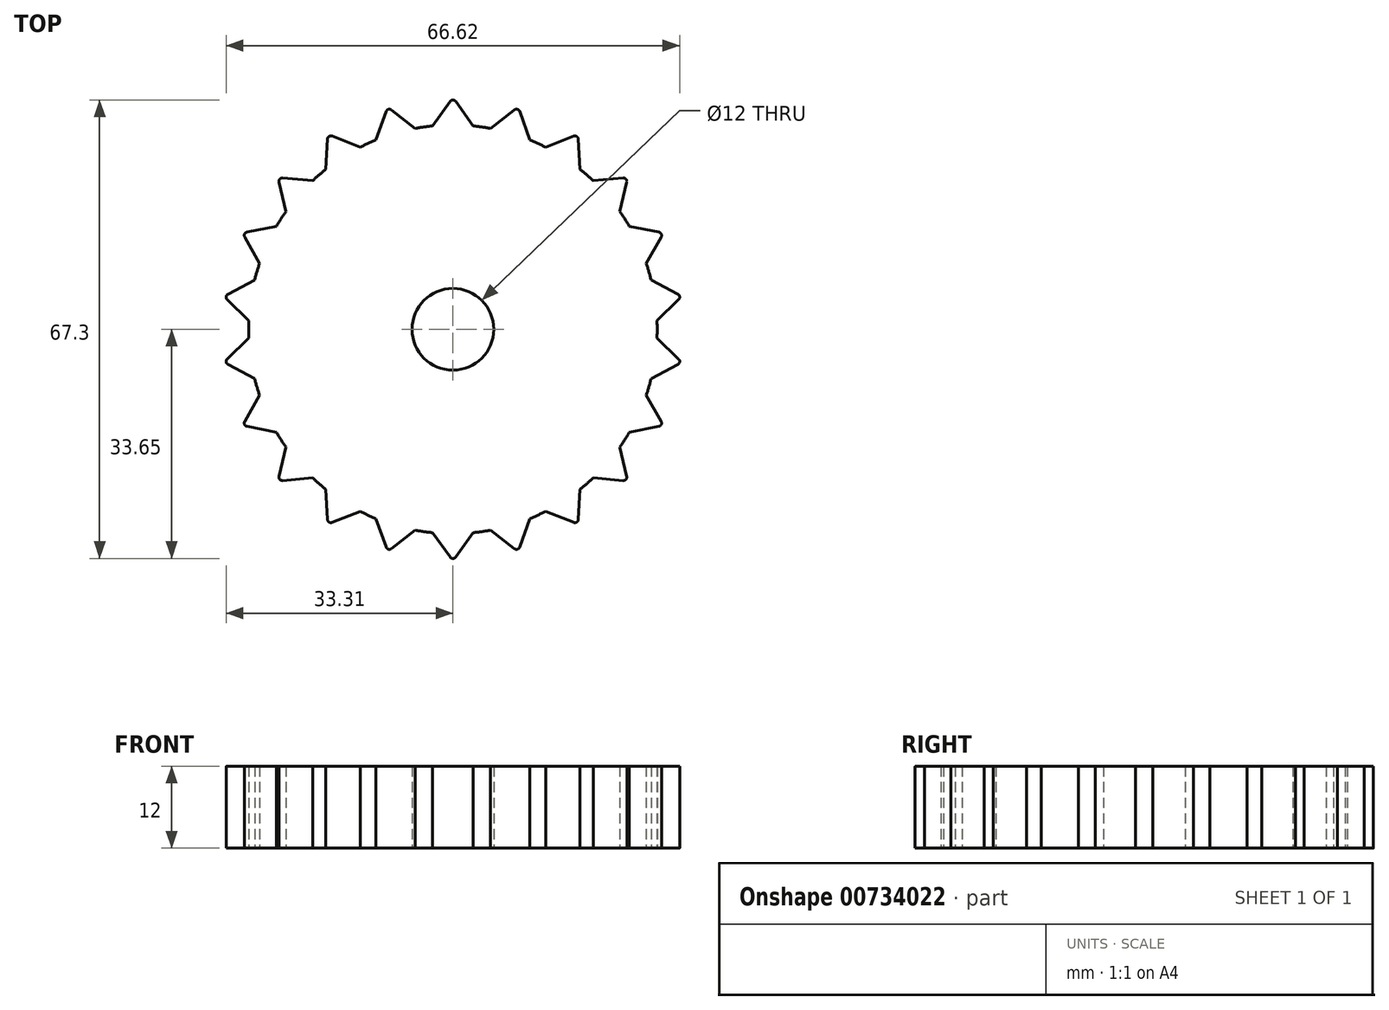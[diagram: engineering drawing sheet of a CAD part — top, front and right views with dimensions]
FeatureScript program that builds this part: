
annotation { "Feature Type Name" : "Feature", "Feature Type Description" : "" }
export const myFeature = defineFeature(function(context is Context, id is Id, definition is map)
    precondition{}
    {
        {
            var Q0;
            Q0=qCreatedBy(makeId("Top.planeOp"),FACE);
            var sketch = newSketch(context, id + "F0", { "sketchPlane" : qUnion([Q0])});
            skArc(sketch, "E0", {"start": v(-24.52, 17.28) * mm, "mid": v(-25.24, 16.22) * mm, "end": v(-25.9, 15.13) * mm});
            skLineSegment(sketch, "E1", {"start": v(-3, 29.85) * mm, "end": v(-0.4, 33.44) * mm});
            skLineSegment(sketch, "E2", {"start": v(0.4, 33.44) * mm, "end": v(3, 29.85) * mm});
            skPoint(sketch, "E3.visualSharp", {"position": v(0, 34) * mm});
            skArc(sketch, "E3.filletArc", {"start": v(0.4, 33.44) * mm, "mid": v(0, 33.65) * mm, "end": v(-0.4, 33.44) * mm});
            skLineSegment(sketch, "E4.1.0", {"start": v(-11.29, 27.8) * mm, "end": v(-9.8, 31.97) * mm});
            skLineSegment(sketch, "E4.1.1", {"start": v(-9.03, 32.2) * mm, "end": v(-5.53, 29.49) * mm});
            skPoint(sketch, "E4.1.2", {"position": v(-9.58, 32.62) * mm});
            skArc(sketch, "E4.1.3", {"start": v(-9.03, 32.2) * mm, "mid": v(-9.48, 32.28) * mm, "end": v(-9.8, 31.97) * mm});
            skLineSegment(sketch, "E4.2.0", {"start": v(-18.66, 23.49) * mm, "end": v(-18.42, 27.91) * mm});
            skLineSegment(sketch, "E4.2.1", {"start": v(-17.74, 28.35) * mm, "end": v(-13.61, 26.73) * mm});
            skPoint(sketch, "E4.2.2", {"position": v(-18.38, 28.6) * mm});
            skArc(sketch, "E4.2.3", {"start": v(-17.74, 28.35) * mm, "mid": v(-18.2, 28.3) * mm, "end": v(-18.42, 27.91) * mm});
            skLineSegment(sketch, "E4.3.0", {"start": v(-24.52, 17.28) * mm, "end": v(-25.54, 21.6) * mm});
            skLineSegment(sketch, "E4.3.1", {"start": v(-25, 22.2) * mm, "end": v(-20.6, 21.81) * mm});
            skPoint(sketch, "E4.3.2", {"position": v(-25.7, 22.27) * mm});
            skArc(sketch, "E4.3.3", {"start": v(-25, 22.2) * mm, "mid": v(-25.43, 22.03) * mm, "end": v(-25.54, 21.6) * mm});
            skLineSegment(sketch, "E4.4.0", {"start": v(-28.4, 9.67) * mm, "end": v(-30.59, 13.52) * mm});
            skLineSegment(sketch, "E4.4.1", {"start": v(-30.25, 14.26) * mm, "end": v(-25.9, 15.13) * mm});
            skPoint(sketch, "E4.4.2", {"position": v(-30.93, 14.12) * mm});
            skArc(sketch, "E4.4.3", {"start": v(-30.25, 14.26) * mm, "mid": v(-30.6, 13.98) * mm, "end": v(-30.59, 13.52) * mm});
            skLineSegment(sketch, "E4.5.0", {"start": v(-29.97, 1.28) * mm, "end": v(-33.16, 4.36) * mm});
            skLineSegment(sketch, "E4.5.1", {"start": v(-33.04, 5.16) * mm, "end": v(-29.12, 7.22) * mm});
            skPoint(sketch, "E4.5.2", {"position": v(-33.65, 4.84) * mm});
            skArc(sketch, "E4.5.3", {"start": v(-33.04, 5.16) * mm, "mid": v(-33.3, 4.79) * mm, "end": v(-33.16, 4.36) * mm});
            skLineSegment(sketch, "E4.6.0", {"start": v(-29.12, -7.22) * mm, "end": v(-33.04, -5.16) * mm});
            skLineSegment(sketch, "E4.6.1", {"start": v(-33.16, -4.36) * mm, "end": v(-29.97, -1.28) * mm});
            skPoint(sketch, "E4.6.2", {"position": v(-33.65, -4.84) * mm});
            skArc(sketch, "E4.6.3", {"start": v(-33.16, -4.36) * mm, "mid": v(-33.3, -4.79) * mm, "end": v(-33.04, -5.16) * mm});
            skLineSegment(sketch, "E4.7.0", {"start": v(-25.9, -15.13) * mm, "end": v(-30.25, -14.26) * mm});
            skLineSegment(sketch, "E4.7.1", {"start": v(-30.59, -13.52) * mm, "end": v(-28.4, -9.67) * mm});
            skPoint(sketch, "E4.7.2", {"position": v(-30.93, -14.12) * mm});
            skArc(sketch, "E4.7.3", {"start": v(-30.59, -13.52) * mm, "mid": v(-30.6, -13.98) * mm, "end": v(-30.25, -14.26) * mm});
            skLineSegment(sketch, "E4.8.0", {"start": v(-20.6, -21.81) * mm, "end": v(-25, -22.2) * mm});
            skLineSegment(sketch, "E4.8.1", {"start": v(-25.54, -21.6) * mm, "end": v(-24.52, -17.28) * mm});
            skPoint(sketch, "E4.8.2", {"position": v(-25.7, -22.27) * mm});
            skArc(sketch, "E4.8.3", {"start": v(-25.54, -21.6) * mm, "mid": v(-25.43, -22.03) * mm, "end": v(-25, -22.2) * mm});
            skLineSegment(sketch, "E4.9.0", {"start": v(-13.61, -26.73) * mm, "end": v(-17.74, -28.35) * mm});
            skLineSegment(sketch, "E4.9.1", {"start": v(-18.42, -27.91) * mm, "end": v(-18.66, -23.49) * mm});
            skPoint(sketch, "E4.9.2", {"position": v(-18.38, -28.6) * mm});
            skArc(sketch, "E4.9.3", {"start": v(-18.42, -27.91) * mm, "mid": v(-18.2, -28.3) * mm, "end": v(-17.74, -28.35) * mm});
            skLineSegment(sketch, "E4.10.0", {"start": v(-5.53, -29.49) * mm, "end": v(-9.03, -32.2) * mm});
            skLineSegment(sketch, "E4.10.1", {"start": v(-9.8, -31.97) * mm, "end": v(-11.29, -27.8) * mm});
            skPoint(sketch, "E4.10.2", {"position": v(-9.58, -32.62) * mm});
            skArc(sketch, "E4.10.3", {"start": v(-9.8, -31.97) * mm, "mid": v(-9.48, -32.28) * mm, "end": v(-9.03, -32.2) * mm});
            skLineSegment(sketch, "E4.11.0", {"start": v(3, -29.85) * mm, "end": v(0.4, -33.44) * mm});
            skLineSegment(sketch, "E4.11.1", {"start": v(-0.4, -33.44) * mm, "end": v(-3, -29.85) * mm});
            skPoint(sketch, "E4.11.2", {"position": v(0, -34) * mm});
            skArc(sketch, "E4.11.3", {"start": v(-0.4, -33.44) * mm, "mid": v(0, -33.65) * mm, "end": v(0.4, -33.44) * mm});
            skLineSegment(sketch, "E4.12.0", {"start": v(11.29, -27.8) * mm, "end": v(9.8, -31.97) * mm});
            skLineSegment(sketch, "E4.12.1", {"start": v(9.03, -32.2) * mm, "end": v(5.53, -29.49) * mm});
            skPoint(sketch, "E4.12.2", {"position": v(9.58, -32.62) * mm});
            skArc(sketch, "E4.12.3", {"start": v(9.03, -32.2) * mm, "mid": v(9.48, -32.28) * mm, "end": v(9.8, -31.97) * mm});
            skLineSegment(sketch, "E4.13.0", {"start": v(18.66, -23.49) * mm, "end": v(18.42, -27.91) * mm});
            skLineSegment(sketch, "E4.13.1", {"start": v(17.74, -28.35) * mm, "end": v(13.61, -26.73) * mm});
            skPoint(sketch, "E4.13.2", {"position": v(18.38, -28.6) * mm});
            skArc(sketch, "E4.13.3", {"start": v(17.74, -28.35) * mm, "mid": v(18.2, -28.3) * mm, "end": v(18.42, -27.91) * mm});
            skLineSegment(sketch, "E4.14.0", {"start": v(24.52, -17.28) * mm, "end": v(25.54, -21.6) * mm});
            skLineSegment(sketch, "E4.14.1", {"start": v(25, -22.2) * mm, "end": v(20.6, -21.81) * mm});
            skPoint(sketch, "E4.14.2", {"position": v(25.7, -22.27) * mm});
            skArc(sketch, "E4.14.3", {"start": v(25, -22.2) * mm, "mid": v(25.43, -22.03) * mm, "end": v(25.54, -21.6) * mm});
            skLineSegment(sketch, "E4.15.0", {"start": v(28.4, -9.67) * mm, "end": v(30.59, -13.52) * mm});
            skLineSegment(sketch, "E4.15.1", {"start": v(30.25, -14.26) * mm, "end": v(25.9, -15.13) * mm});
            skPoint(sketch, "E4.15.2", {"position": v(30.93, -14.12) * mm});
            skArc(sketch, "E4.15.3", {"start": v(30.25, -14.26) * mm, "mid": v(30.6, -13.98) * mm, "end": v(30.59, -13.52) * mm});
            skLineSegment(sketch, "E4.16.0", {"start": v(29.97, -1.28) * mm, "end": v(33.16, -4.36) * mm});
            skLineSegment(sketch, "E4.16.1", {"start": v(33.04, -5.16) * mm, "end": v(29.12, -7.22) * mm});
            skPoint(sketch, "E4.16.2", {"position": v(33.65, -4.84) * mm});
            skArc(sketch, "E4.16.3", {"start": v(33.04, -5.16) * mm, "mid": v(33.3, -4.79) * mm, "end": v(33.16, -4.36) * mm});
            skLineSegment(sketch, "E4.17.0", {"start": v(29.12, 7.22) * mm, "end": v(33.04, 5.16) * mm});
            skLineSegment(sketch, "E4.17.1", {"start": v(33.16, 4.36) * mm, "end": v(29.97, 1.28) * mm});
            skPoint(sketch, "E4.17.2", {"position": v(33.65, 4.84) * mm});
            skArc(sketch, "E4.17.3", {"start": v(33.16, 4.36) * mm, "mid": v(33.3, 4.79) * mm, "end": v(33.04, 5.16) * mm});
            skLineSegment(sketch, "E4.18.0", {"start": v(25.9, 15.13) * mm, "end": v(30.25, 14.26) * mm});
            skLineSegment(sketch, "E4.18.1", {"start": v(30.59, 13.52) * mm, "end": v(28.4, 9.67) * mm});
            skPoint(sketch, "E4.18.2", {"position": v(30.93, 14.12) * mm});
            skArc(sketch, "E4.18.3", {"start": v(30.59, 13.52) * mm, "mid": v(30.6, 13.98) * mm, "end": v(30.25, 14.26) * mm});
            skLineSegment(sketch, "E4.19.0", {"start": v(20.6, 21.81) * mm, "end": v(25, 22.2) * mm});
            skLineSegment(sketch, "E4.19.1", {"start": v(25.54, 21.6) * mm, "end": v(24.52, 17.28) * mm});
            skPoint(sketch, "E4.19.2", {"position": v(25.7, 22.27) * mm});
            skArc(sketch, "E4.19.3", {"start": v(25.54, 21.6) * mm, "mid": v(25.43, 22.03) * mm, "end": v(25, 22.2) * mm});
            skLineSegment(sketch, "E4.20.0", {"start": v(13.61, 26.73) * mm, "end": v(17.74, 28.35) * mm});
            skLineSegment(sketch, "E4.20.1", {"start": v(18.42, 27.91) * mm, "end": v(18.66, 23.49) * mm});
            skPoint(sketch, "E4.20.2", {"position": v(18.38, 28.6) * mm});
            skArc(sketch, "E4.20.3", {"start": v(18.42, 27.91) * mm, "mid": v(18.2, 28.3) * mm, "end": v(17.74, 28.35) * mm});
            skLineSegment(sketch, "E4.21.0", {"start": v(5.53, 29.49) * mm, "end": v(9.03, 32.2) * mm});
            skLineSegment(sketch, "E4.21.1", {"start": v(9.8, 31.97) * mm, "end": v(11.29, 27.8) * mm});
            skPoint(sketch, "E4.21.2", {"position": v(9.58, 32.62) * mm});
            skArc(sketch, "E4.21.3", {"start": v(9.8, 31.97) * mm, "mid": v(9.48, 32.28) * mm, "end": v(9.03, 32.2) * mm});
            skCircle(sketch, "E5", {"center": v(0, 0) * mm, "radius": 34 * mm, "construction": true});
            skArc(sketch, "E6.trimOffspring", {"start": v(-18.66, 23.49) * mm, "mid": v(-19.65, 22.67) * mm, "end": v(-20.6, 21.81) * mm});
            skArc(sketch, "E7.trimOffspring", {"start": v(-11.29, 27.8) * mm, "mid": v(-12.46, 27.29) * mm, "end": v(-13.61, 26.73) * mm});
            skArc(sketch, "E8.trimOffspring", {"start": v(-3, 29.85) * mm, "mid": v(-4.27, 29.7) * mm, "end": v(-5.53, 29.49) * mm});
            skArc(sketch, "E9.trimOffspring", {"start": v(5.53, 29.49) * mm, "mid": v(4.27, 29.7) * mm, "end": v(3, 29.85) * mm});
            skArc(sketch, "E10.trimOffspring", {"start": v(13.61, 26.73) * mm, "mid": v(12.46, 27.29) * mm, "end": v(11.29, 27.8) * mm});
            skArc(sketch, "E11.trimOffspring", {"start": v(20.6, 21.81) * mm, "mid": v(19.65, 22.67) * mm, "end": v(18.66, 23.49) * mm});
            skArc(sketch, "E12.trimOffspring", {"start": v(25.9, 15.13) * mm, "mid": v(25.24, 16.22) * mm, "end": v(24.52, 17.28) * mm});
            skArc(sketch, "E13.trimOffspring", {"start": v(29.12, 7.22) * mm, "mid": v(28.78, 8.45) * mm, "end": v(28.4, 9.67) * mm});
            skArc(sketch, "E14.trimOffspring", {"start": v(29.97, -1.28) * mm, "mid": v(30, 0) * mm, "end": v(29.97, 1.28) * mm});
            skArc(sketch, "E15.trimOffspring", {"start": v(28.4, -9.67) * mm, "mid": v(28.78, -8.45) * mm, "end": v(29.12, -7.22) * mm});
            skArc(sketch, "E16.trimOffspring", {"start": v(24.52, -17.28) * mm, "mid": v(25.24, -16.22) * mm, "end": v(25.9, -15.13) * mm});
            skArc(sketch, "E17.trimOffspring", {"start": v(18.66, -23.49) * mm, "mid": v(19.65, -22.67) * mm, "end": v(20.6, -21.81) * mm});
            skArc(sketch, "E18.trimOffspring", {"start": v(11.29, -27.8) * mm, "mid": v(12.46, -27.29) * mm, "end": v(13.61, -26.73) * mm});
            skArc(sketch, "E19.trimOffspring", {"start": v(3, -29.85) * mm, "mid": v(4.27, -29.7) * mm, "end": v(5.53, -29.49) * mm});
            skArc(sketch, "E20.trimOffspring", {"start": v(-5.53, -29.49) * mm, "mid": v(-4.27, -29.7) * mm, "end": v(-3, -29.85) * mm});
            skArc(sketch, "E21.trimOffspring", {"start": v(-13.61, -26.73) * mm, "mid": v(-12.46, -27.29) * mm, "end": v(-11.29, -27.8) * mm});
            skArc(sketch, "E22.trimOffspring", {"start": v(-20.6, -21.81) * mm, "mid": v(-19.65, -22.67) * mm, "end": v(-18.66, -23.49) * mm});
            skArc(sketch, "E23.trimOffspring", {"start": v(-25.9, -15.13) * mm, "mid": v(-25.24, -16.22) * mm, "end": v(-24.52, -17.28) * mm});
            skArc(sketch, "E24.trimOffspring", {"start": v(-29.12, -7.22) * mm, "mid": v(-28.78, -8.45) * mm, "end": v(-28.4, -9.67) * mm});
            skArc(sketch, "E25.trimOffspring", {"start": v(-29.97, 1.28) * mm, "mid": v(-30, 0) * mm, "end": v(-29.97, -1.28) * mm});
            skArc(sketch, "E26.trimOffspring", {"start": v(-28.4, 9.67) * mm, "mid": v(-28.78, 8.45) * mm, "end": v(-29.12, 7.22) * mm});
            skSolve(sketch);
        }
        {
            var Q0;
            Q0 = qSketchRegion(id + "F0", true);
            extrude(context, id + "F1", {"entities" : qUnion([Q0]), "endBound" : BoundingType.SYMMETRIC, "depth" : 12 * mm, "offsetDistance" : 25 * mm});
        }
        {
            var Q0;
            Q0=makeQuery(id+"F1.opExtrude","CAP_FACE",FACE,{"disambiguationData":[OSD([sQuery(id+"F0.wireOp",EDGE,"E0"),sQuery(id+"F0.wireOp",EDGE,"E1"),sQuery(id+"F0.wireOp",EDGE,"E2"),sQuery(id+"F0.wireOp",EDGE,"E3.filletArc"),sQuery(id+"F0.wireOp",EDGE,"E4.1.0"),sQuery(id+"F0.wireOp",EDGE,"E4.1.1"),sQuery(id+"F0.wireOp",EDGE,"E4.1.3"),sQuery(id+"F0.wireOp",EDGE,"E4.2.0"),sQuery(id+"F0.wireOp",EDGE,"E4.2.1"),sQuery(id+"F0.wireOp",EDGE,"E4.2.3"),sQuery(id+"F0.wireOp",EDGE,"E4.3.0"),sQuery(id+"F0.wireOp",EDGE,"E4.3.1"),sQuery(id+"F0.wireOp",EDGE,"E4.3.3"),sQuery(id+"F0.wireOp",EDGE,"E4.4.0"),sQuery(id+"F0.wireOp",EDGE,"E4.4.1"),sQuery(id+"F0.wireOp",EDGE,"E4.4.3"),sQuery(id+"F0.wireOp",EDGE,"E4.5.0"),sQuery(id+"F0.wireOp",EDGE,"E4.5.1"),sQuery(id+"F0.wireOp",EDGE,"E4.5.3"),sQuery(id+"F0.wireOp",EDGE,"E4.6.0"),sQuery(id+"F0.wireOp",EDGE,"E4.6.1"),sQuery(id+"F0.wireOp",EDGE,"E4.6.3"),sQuery(id+"F0.wireOp",EDGE,"E4.7.0"),sQuery(id+"F0.wireOp",EDGE,"E4.7.1"),sQuery(id+"F0.wireOp",EDGE,"E4.7.3"),sQuery(id+"F0.wireOp",EDGE,"E4.8.0"),sQuery(id+"F0.wireOp",EDGE,"E4.8.1"),sQuery(id+"F0.wireOp",EDGE,"E4.8.3"),sQuery(id+"F0.wireOp",EDGE,"E4.9.0"),sQuery(id+"F0.wireOp",EDGE,"E4.9.1"),sQuery(id+"F0.wireOp",EDGE,"E4.9.3"),sQuery(id+"F0.wireOp",EDGE,"E4.10.0"),sQuery(id+"F0.wireOp",EDGE,"E4.10.1"),sQuery(id+"F0.wireOp",EDGE,"E4.10.3"),sQuery(id+"F0.wireOp",EDGE,"E4.11.0"),sQuery(id+"F0.wireOp",EDGE,"E4.11.1"),sQuery(id+"F0.wireOp",EDGE,"E4.11.3"),sQuery(id+"F0.wireOp",EDGE,"E4.12.0"),sQuery(id+"F0.wireOp",EDGE,"E4.12.1"),sQuery(id+"F0.wireOp",EDGE,"E4.12.3"),sQuery(id+"F0.wireOp",EDGE,"E4.13.0"),sQuery(id+"F0.wireOp",EDGE,"E4.13.1"),sQuery(id+"F0.wireOp",EDGE,"E4.13.3"),sQuery(id+"F0.wireOp",EDGE,"E4.14.0"),sQuery(id+"F0.wireOp",EDGE,"E4.14.1"),sQuery(id+"F0.wireOp",EDGE,"E4.14.3"),sQuery(id+"F0.wireOp",EDGE,"E4.15.0"),sQuery(id+"F0.wireOp",EDGE,"E4.15.1"),sQuery(id+"F0.wireOp",EDGE,"E4.15.3"),sQuery(id+"F0.wireOp",EDGE,"E4.16.0"),sQuery(id+"F0.wireOp",EDGE,"E4.16.1"),sQuery(id+"F0.wireOp",EDGE,"E4.16.3"),sQuery(id+"F0.wireOp",EDGE,"E4.17.0"),sQuery(id+"F0.wireOp",EDGE,"E4.17.1"),sQuery(id+"F0.wireOp",EDGE,"E4.17.3"),sQuery(id+"F0.wireOp",EDGE,"E4.18.0"),sQuery(id+"F0.wireOp",EDGE,"E4.18.1"),sQuery(id+"F0.wireOp",EDGE,"E4.18.3"),sQuery(id+"F0.wireOp",EDGE,"E4.19.0"),sQuery(id+"F0.wireOp",EDGE,"E4.19.1"),sQuery(id+"F0.wireOp",EDGE,"E4.19.3"),sQuery(id+"F0.wireOp",EDGE,"E4.20.0"),sQuery(id+"F0.wireOp",EDGE,"E4.20.1"),sQuery(id+"F0.wireOp",EDGE,"E4.20.3"),sQuery(id+"F0.wireOp",EDGE,"E4.21.0"),sQuery(id+"F0.wireOp",EDGE,"E4.21.1"),sQuery(id+"F0.wireOp",EDGE,"E4.21.3"),sQuery(id+"F0.wireOp",EDGE,"E6.trimOffspring"),sQuery(id+"F0.wireOp",EDGE,"E7.trimOffspring"),sQuery(id+"F0.wireOp",EDGE,"E8.trimOffspring"),sQuery(id+"F0.wireOp",EDGE,"E9.trimOffspring"),sQuery(id+"F0.wireOp",EDGE,"E10.trimOffspring"),sQuery(id+"F0.wireOp",EDGE,"E11.trimOffspring"),sQuery(id+"F0.wireOp",EDGE,"E12.trimOffspring"),sQuery(id+"F0.wireOp",EDGE,"E13.trimOffspring"),sQuery(id+"F0.wireOp",EDGE,"E14.trimOffspring"),sQuery(id+"F0.wireOp",EDGE,"E15.trimOffspring"),sQuery(id+"F0.wireOp",EDGE,"E16.trimOffspring"),sQuery(id+"F0.wireOp",EDGE,"E17.trimOffspring"),sQuery(id+"F0.wireOp",EDGE,"E18.trimOffspring"),sQuery(id+"F0.wireOp",EDGE,"E19.trimOffspring"),sQuery(id+"F0.wireOp",EDGE,"E20.trimOffspring"),sQuery(id+"F0.wireOp",EDGE,"E21.trimOffspring"),sQuery(id+"F0.wireOp",EDGE,"E22.trimOffspring"),sQuery(id+"F0.wireOp",EDGE,"E23.trimOffspring"),sQuery(id+"F0.wireOp",EDGE,"E24.trimOffspring"),sQuery(id+"F0.wireOp",EDGE,"E25.trimOffspring"),sQuery(id+"F0.wireOp",EDGE,"E26.trimOffspring")])],"isStart":true});
            var sketch = newSketch(context, id + "F2", { "sketchPlane" : qUnion([Q0])});
            skCircle(sketch, "E27", {"center": v(0, 0) * mm, "radius": 6 * mm});
            skSolve(sketch);
        }
        {
            var Q0;
            Q0 = qSketchRegion(id + "F2", true);
            extrude(context, id + "F3", {"entities" : qUnion([Q0]), "operationType" : NewBodyOperationType.REMOVE, "oppositeDirection" : true, "depth" : 25 * mm, "offsetDistance" : 25 * mm});
        }
    });
